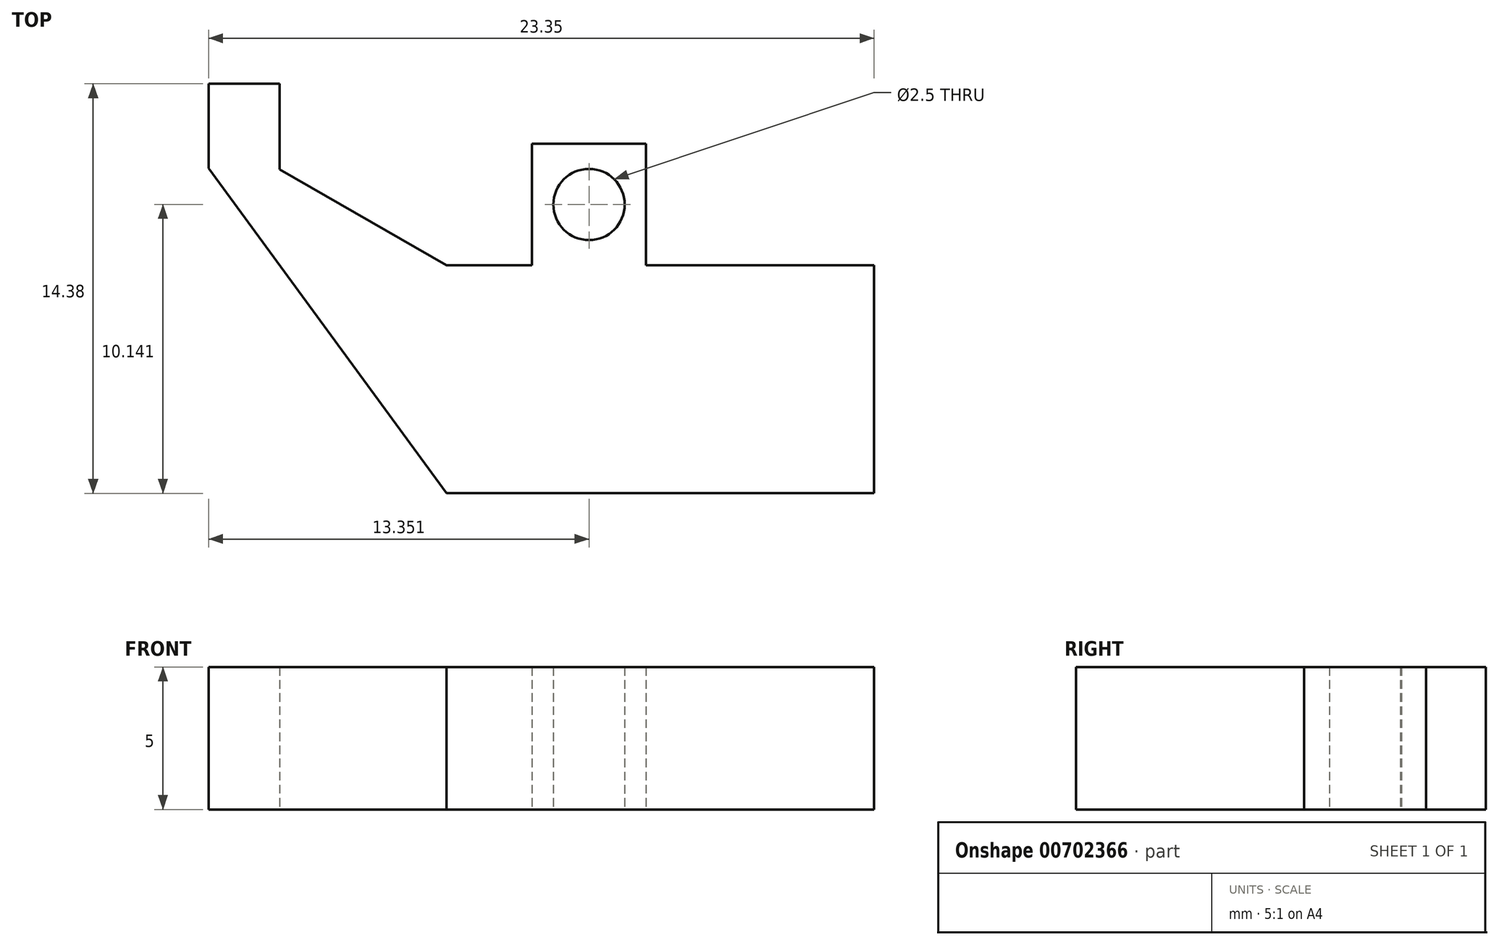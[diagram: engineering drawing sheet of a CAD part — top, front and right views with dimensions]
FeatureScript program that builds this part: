
annotation { "Feature Type Name" : "Feature", "Feature Type Description" : "" }
export const myFeature = defineFeature(function(context is Context, id is Id, definition is map)
    precondition{}
    {
        {
            var Q0;
            Q0=qCreatedBy(makeId("Top.planeOp"),FACE);
            var sketch = newSketch(context, id + "F0", { "sketchPlane" : qUnion([Q0])});
            skLineSegment(sketch, "E0", {"start": v(-0.43, 2.58) * mm, "end": v(-0.43, 6.86) * mm});
            skLineSegment(sketch, "E1", {"start": v(-0.43, 6.86) * mm, "end": v(-4.43, 6.86) * mm});
            skLineSegment(sketch, "E2", {"start": v(-4.43, 6.86) * mm, "end": v(-4.43, 2.58) * mm});
            skLineSegment(sketch, "E3", {"start": v(-4.43, 6.86) * mm, "end": v(-0.43, 2.58) * mm, "construction": true});
            skLineSegment(sketch, "E4", {"start": v(-0.43, 6.86) * mm, "end": v(-4.43, 2.58) * mm, "construction": true});
            skCircle(sketch, "E5", {"center": v(-2.43, 4.72) * mm, "radius": 1.25 * mm});
            skLineSegment(sketch, "E6", {"start": v(-13.28, 5.96) * mm, "end": v(-13.28, 8.96) * mm});
            skLineSegment(sketch, "E7", {"start": v(-13.28, 8.96) * mm, "end": v(-15.78, 8.96) * mm});
            skLineSegment(sketch, "E8", {"start": v(-15.78, 8.96) * mm, "end": v(-15.78, 6) * mm});
            skLineSegment(sketch, "E9", {"start": v(-15.78, 6) * mm, "end": v(-7.43, -5.42) * mm});
            skLineSegment(sketch, "E10", {"start": v(-13.28, 5.96) * mm, "end": v(-7.43, 2.58) * mm});
            skLineSegment(sketch, "E11", {"start": v(-7.43, 2.58) * mm, "end": v(-4.43, 2.58) * mm});
            skLineSegment(sketch, "E12", {"start": v(7.57, 2.58) * mm, "end": v(7.57, -5.42) * mm});
            skLineSegment(sketch, "E13", {"start": v(-7.43, -5.42) * mm, "end": v(7.57, -5.42) * mm});
            skLineSegment(sketch, "E14", {"start": v(-0.43, 2.58) * mm, "end": v(7.57, 2.58) * mm});
            skSolve(sketch);
        }
        {
            var Q0;
            Q0=makeQuery(id+"F0.imprint","IMPRINT",FACE,{"disambiguationData":[TD([[makeQuery(id+"F0.imprint","IMPRINT",EDGE,{"derivedFrom":sQuery(id+"F0.wireOp",EDGE,"E0")}),1.0]])]});
            extrude(context, id + "F1", {"entities" : qUnion([Q0]), "depth" : 5 * mm, "offsetDistance" : 25 * mm});
        }
    });
